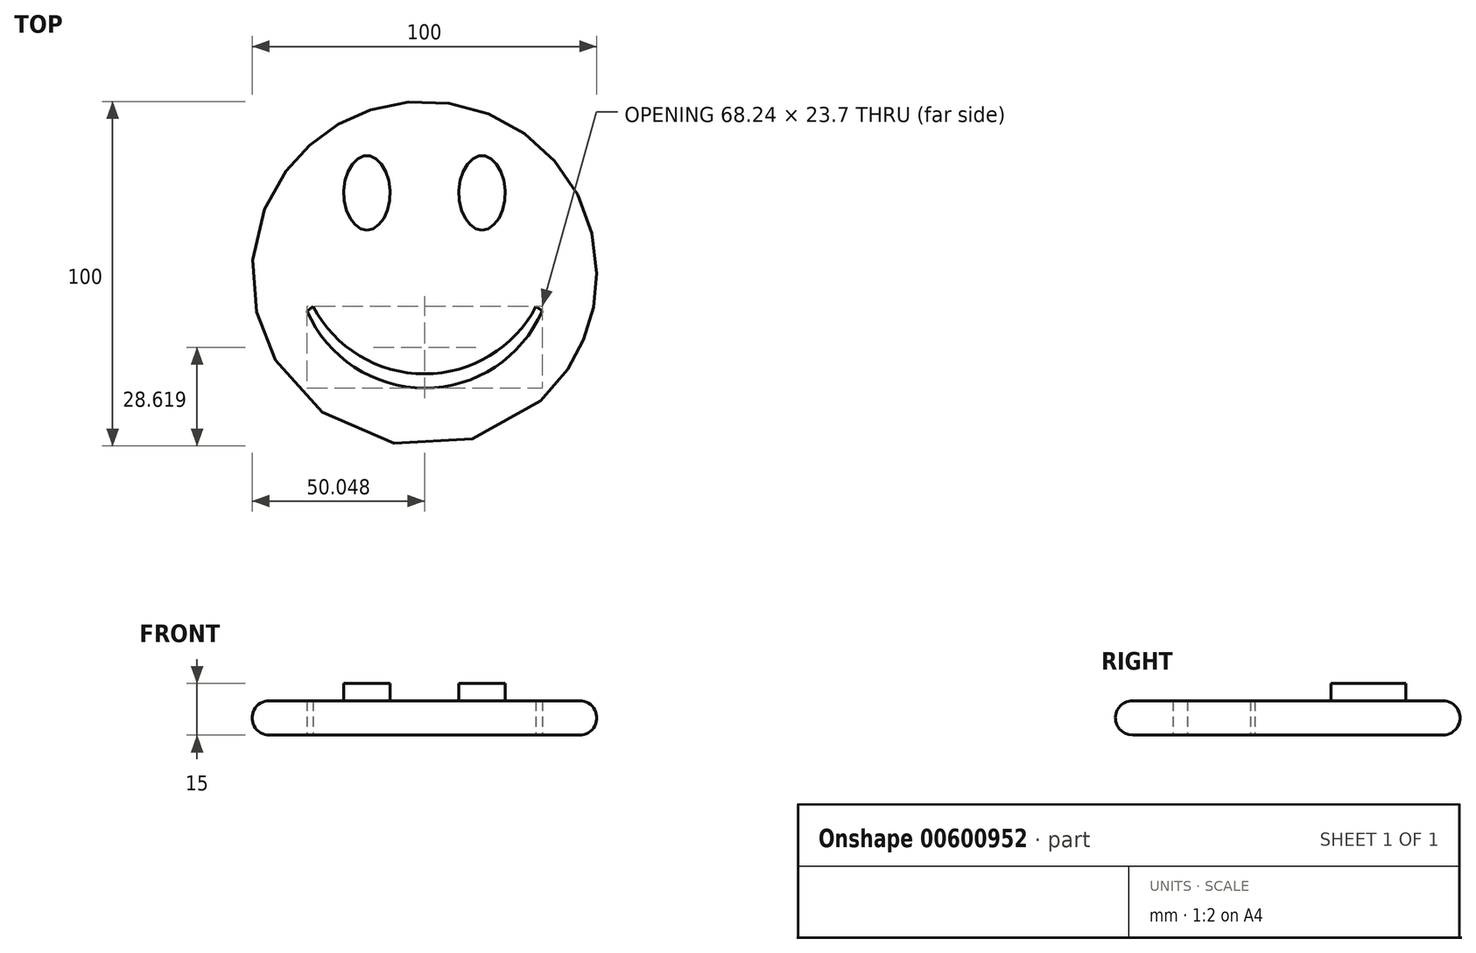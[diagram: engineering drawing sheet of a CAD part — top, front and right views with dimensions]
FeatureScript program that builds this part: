
annotation { "Feature Type Name" : "Feature", "Feature Type Description" : "" }
export const myFeature = defineFeature(function(context is Context, id is Id, definition is map)
    precondition{}
    {
        {
            var Q0;
            Q0=qCreatedBy(makeId("Top.planeOp"),FACE);
            var sketch = newSketch(context, id + "F0", { "sketchPlane" : qUnion([Q0])});
            skEllipse(sketch, "E0", {"center": v(-16.7, 23.43) * mm, "majorRadius": 10.81 * mm, "minorRadius": 6.7 * mm, "majorAxis": v(0, -1)});
            skEllipse(sketch, "E1.MirrorC", {"center": v(16.7, 23.43) * mm, "majorRadius": 10.81 * mm, "minorRadius": 6.7 * mm, "majorAxis": v(0, -1)});
            skSolve(sketch);
        }
        {
            var Q0;
            Q0=qCreatedBy(makeId("Top.planeOp"),FACE);
            var sketch = newSketch(context, id + "F1", { "sketchPlane" : qUnion([Q0])});
            skCircle(sketch, "E2", {"center": v(0, 0) * mm, "radius": 50 * mm});
            skPoint(sketch, "E2.first.point", {"position": v(0, 50) * mm});
            skPoint(sketch, "E2.second.point", {"position": v(0, -50) * mm});
            skPoint(sketch, "E2.third.point", {"position": v(50, 0) * mm});
            skSolve(sketch);
        }
        {
            var Q0;
            Q0=qCreatedBy(makeId("Top.planeOp"),FACE);
            var sketch = newSketch(context, id + "F2", { "sketchPlane" : qUnion([Q0])});
            skArc(sketch, "E3", {"start": v(-34.07, -10.83) * mm, "mid": v(-33.18, -10.22) * mm, "end": v(-32.34, -9.53) * mm});
            skArc(sketch, "E4", {"start": v(-32.34, -9.53) * mm, "mid": v(0, -29.12) * mm, "end": v(32.37, -9.56) * mm});
            skArc(sketch, "E5", {"start": v(-34.07, -10.83) * mm, "mid": v(0.05, -33.23) * mm, "end": v(34.17, -10.84) * mm});
            skLineSegment(sketch, "E6", {"start": v(32.37, -9.56) * mm, "end": v(34.17, -10.84) * mm});
            skSolve(sketch);
        }
        {
            var Q0;
            Q0=makeQuery(id+"F1.imprint","IMPRINT",FACE,{"disambiguationData":[TD([[makeQuery(id+"F1.imprint","IMPRINT",EDGE,{"derivedFrom":sQuery(id+"F1.wireOp",EDGE,"E2")}),1.0]])]});
            extrude(context, id + "F3", {"entities" : qUnion([Q0]), "depth" : 10 * mm, "offsetDistance" : 25.4 * mm});
        }
        {
            var Q0;
            Q0 = qSketchRegion(id + "F2", true);
            extrude(context, id + "F4", {"entities" : qUnion([Q0]), "operationType" : NewBodyOperationType.REMOVE, "endBound" : BoundingType.UP_TO_NEXT, "depth" : 9.2 * mm, "offsetDistance" : 25 * mm});
        }
        {
            var Q0;
            Q0 = qSketchRegion(id + "F0", true);
            extrude(context, id + "F5", {"entities" : qUnion([Q0]), "operationType" : NewBodyOperationType.ADD, "depth" : 15 * mm, "offsetDistance" : 25 * mm});
        }
        {
            var Q0;
            Q0=makeQuery(id+"F3.opExtrude","CAP_EDGE",EDGE,{"disambiguationData":[OSD([sQuery(id+"F1.wireOp",EDGE,"E2")])],"isStart":false});
            var Q1;
            Q1=makeQuery(id+"F3.opExtrude","CAP_EDGE",EDGE,{"disambiguationData":[OSD([sQuery(id+"F1.wireOp",EDGE,"E2")])],"isStart":true});
            fillet(context, id + "F6", {"entities" : qUnion([Q0, Q1]), "radius" : 5 * mm, "tangentPropagation" : true, "allowEdgeOverflow" : false});
        }
    });
